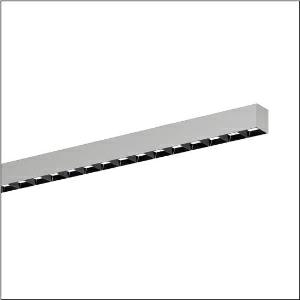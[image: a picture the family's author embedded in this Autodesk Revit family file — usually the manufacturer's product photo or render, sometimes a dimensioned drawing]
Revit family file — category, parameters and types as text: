
# Revit family: silica_r__21_51mx22tat4s_f26d
name_source: partatom
category: Lighting Fixtures
units: mm (PartAtom-declared; Revit-internal decimal feet)

## family parameters
Cut with Voids When Loaded = No
Host = Face
Light Source = No
Part Type = Normal
Room Calculation Point = No
Round Connector Dimension = Use Diameter
Shared = No

## types (1)
- --- (1 x LED, 3720 lm, 32.1 W, 6500K)
    Apparent Load = 32 VA
    CIE Flux Codes = 84 100 100 100 100
    Color Rendering = 80
    Color Temperature = 6500K
    Default Elevation = 1800 mm
    Description = Silica® 21, office luminaire, primary light control with darklight reflector, of PMMA, black, CAT 2 (L<= 3000cd/m²), light emission: direct distribution, primary light characteristic: symmetric, installation type: surface-mounted, LED, rated luminous flux: 3.720lm, luminous efficacy: 110lm/W, light colour: 8tw, colour temperature: 2700..6500K, control gear: ECG DALI, with terminal, 3+2-pole, max. 2.5mm², mains connection: 220..240V, AC, 50/60Hz, rated input power: 33.8W, luminaire housing, of aluminium, metallic grey (RAL 9006), length: 1.204mm, width: 53mm, height: 53mm, protection rating (complete): IP20, insulation class (complete): insulation class I (protective earthing), certification: CE, permissible operating ambient temperature: 0..+35°C, standard: EN 50419, packaging unit: 1 piece
    Height = 0 mm  [stored 0 ft]
    Lamp = 1 x LED
    Lamp Light Flux = 3720 lm
    Lamp Power = 32.1 W
    Lamp count = 1
    Length = 1204 mm
    Luminous efficacy = 116 lm/W
    Manufacturer = Siteco
    ModVariant = No
    Model = 51MX22TAT4S
    Mounting Place = Ceiling
    Mounting Type = Recessed
    Number of Poles = 1
    OnlyDefault = Yes
    Power Factor = 1
    Product Name = Silica® 21
    Product group = office luminaire | ceiling recessed
    ProductGroupID = 400
    Protection Class = Protection class I
    Protection Degree = IP 20
    RLX_Detail_Level = 1
    RLX_Emergency_Light_Flux = 0 lm
    RLX_Emergency_Type = 0
    RLX_Emergency_Type_DB = No
    RlxData = <blob elided: 39233 chars, md5=9667f102>
    Socket = socket
    Standby Power = 0 W
    System Light Flux = 3720 lm
    System Power = 32 W
    Type Comments = individual setting
    Type Image = l_1335929.jpg
    URL = http://relux.com
    VarID = @adj_109927
    Voltage = 0 V
    Weight = 0.00 kg
    Width = 53 mm

note: [stored X ft] marks values corroborated as IEEE doubles in the binary element streams (Revit-internal decimal feet)

## geometry (parser evidence)
native form markers: Blend x4, Sweep x10
no freeform markers — native parametric forms only
